# Revit family: ContinuousSpouting_RainwaterHead_MailBox-With Bead
name_source: partatom
category: Plumbing Fixtures
revit_build: Autodesk Revit 2013 (Build: 20121003_2115(x64)
units: mm (PartAtom-declared; Revit-internal decimal feet)

## types (5) — shared parameters
Distance from Wall = 20 mm  [stored 0.0656168 ft]
Downpipe Offset = 100 mm  [stored 0.328084 ft]
Downpipe Radius = 40 mm  [stored 0.131234 ft]
Hole Radius = 38 mm  [stored 0.124672 ft]
Manufacturer = Continuous Group NZ Ltd
Model = Mail Box
Outlet Width = 140 mm  [stored 0.459318 ft]
Type Comments = Rainwater Head
URL = http://www.continuous.co.nz
Width = 300 mm

## per-type parameters (varying)
| type | Depth | Height | Lip Width | Rainwater Head |
| Continuous Spouting - Mail Box (Copper) | 150 mm | 300 mm | 25 mm  [stored 0.082021 ft] | CS-Copper |
| Continuous Spouting - Mail Box (Colorcote®) | 165 mm | 305 mm  [stored 1.00066 ft] | 10 mm  [stored 0.0328084 ft] | CS-Colorcote® |
| Continuous Spouting - Mail Box (Zinc) | 165 mm | 305 mm  [stored 1.00066 ft] | 10 mm  [stored 0.0328084 ft] | CS-Zinc |
| Continuous Spouting - Mail Box (Unpainted Zincalume) | 165 mm | 305 mm  [stored 1.00066 ft] | 10 mm  [stored 0.0328084 ft] | CS-Unpainted Zincalume |
| Continuous Spouting - Mail Box (Aluminium) | 165 mm | 305 mm  [stored 1.00066 ft] | 10 mm  [stored 0.0328084 ft] | CS-Aluminium |

note: [stored X ft] marks values corroborated as IEEE doubles in the binary element streams (Revit-internal decimal feet)

## geometry (parser evidence)
native form markers: Blend x14, Sweep x2
no freeform markers — native parametric forms only
